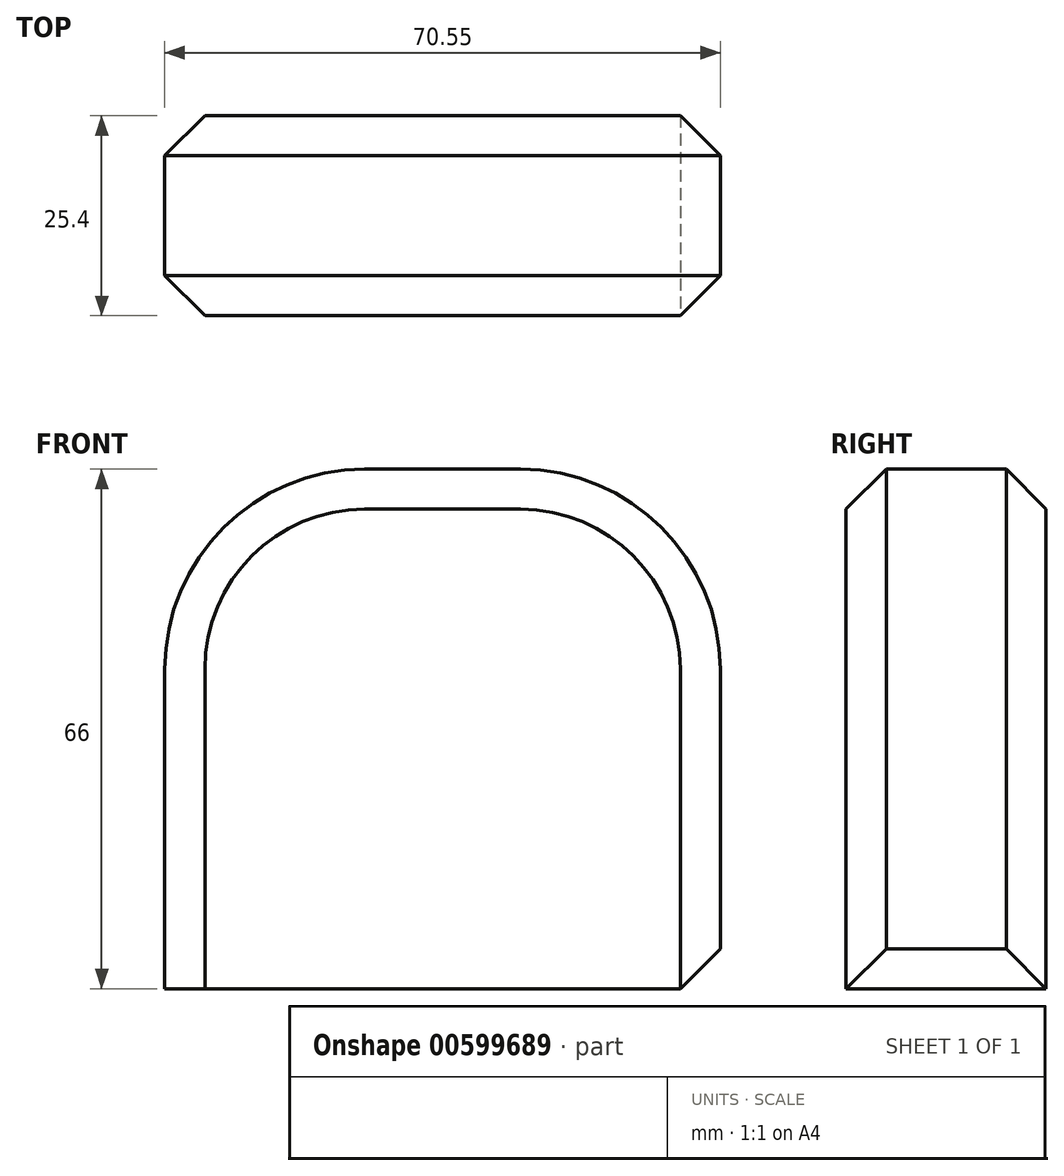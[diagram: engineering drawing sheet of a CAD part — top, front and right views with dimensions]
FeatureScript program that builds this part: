
annotation { "Feature Type Name" : "Feature", "Feature Type Description" : "" }
export const myFeature = defineFeature(function(context is Context, id is Id, definition is map)
    precondition{}
    {
        {
            var Q0;
            Q0=qCreatedBy(makeId("Front.planeOp"),FACE);
            var sketch = newSketch(context, id + "F0", { "sketchPlane" : qUnion([Q0])});
            skLineSegment(sketch, "E0.bottom", {"start": v(0, 0) * mm, "end": v(70.55, 0) * mm});
            skLineSegment(sketch, "E0.top", {"start": v(0, -66) * mm, "end": v(70.55, -66) * mm});
            skLineSegment(sketch, "E0.left", {"start": v(0, 0) * mm, "end": v(0, -66) * mm});
            skLineSegment(sketch, "E0.right", {"start": v(70.55, 0) * mm, "end": v(70.55, -66) * mm});
            skSolve(sketch);
        }
        {
            var Q0;
            Q0=makeQuery(id+"F0.imprint","IMPRINT",FACE,{"disambiguationData":[TD([[makeQuery(id+"F0.imprint","IMPRINT",EDGE,{"derivedFrom":sQuery(id+"F0.wireOp",EDGE,"E0.bottom")}),-1.0]])]});
            extrude(context, id + "F1", {"entities" : qUnion([Q0]), "depth" : 25.4 * mm, "offsetDistance" : 25.4 * mm});
        }
        {
            var Q0;
            Q0=makeQuery(id+"F1.opExtrude","SWEPT_EDGE",EDGE,{"disambiguationData":[OSD([sQuery(id+"F0.wireOp",EDGE,"E0.bottom"),sQuery(id+"F0.wireOp",EDGE,"E0.right")])]});
            var Q1;
            Q1=makeQuery(id+"F1.opExtrude","SWEPT_EDGE",EDGE,{"disambiguationData":[OSD([sQuery(id+"F0.wireOp",EDGE,"E0.bottom"),sQuery(id+"F0.wireOp",EDGE,"E0.left")])]});
            fillet(context, id + "F2", {"entities" : qUnion([Q0, Q1]), "radius" : 25.4 * mm, "tangentPropagation" : true, "allowEdgeOverflow" : false});
        }
        {
            var Q0;
            Q0=makeQuery(id+"F1.opExtrude","SWEPT_FACE",FACE,{"disambiguationData":[OSD([sQuery(id+"F0.wireOp",EDGE,"E0.right")])]});
            chamfer(context, id + "F3", {"entities" : qUnion([Q0]), "width" : 5.08 * mm, "tangentPropagation" : true});
        }
    });
